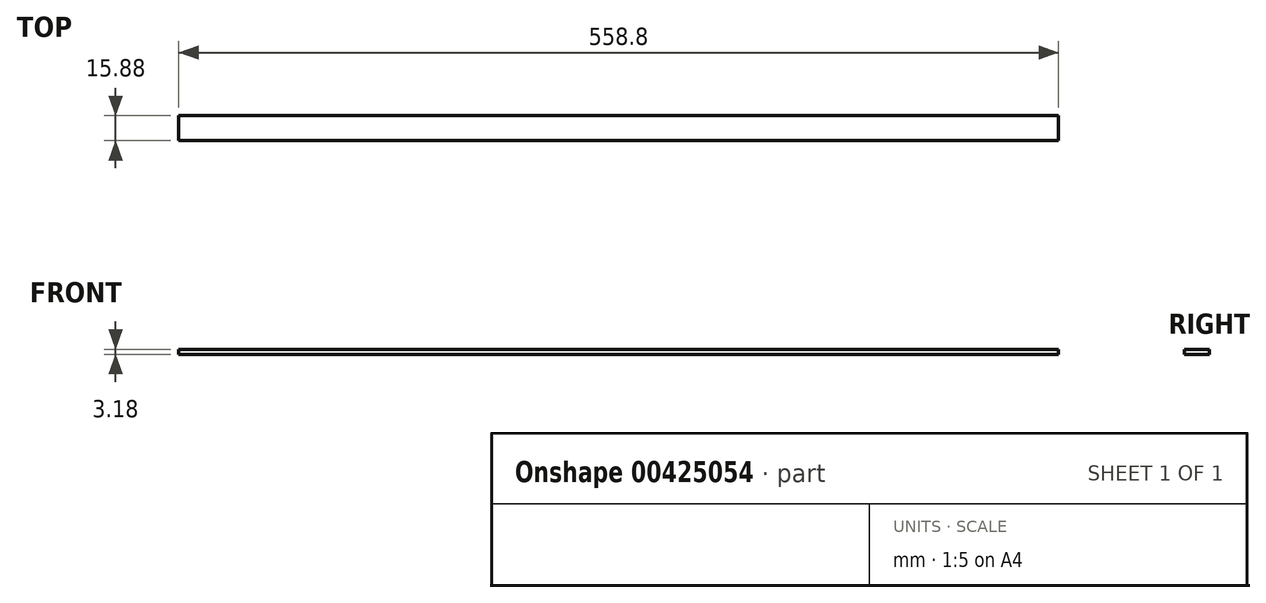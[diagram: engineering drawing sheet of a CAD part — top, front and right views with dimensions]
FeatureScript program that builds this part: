
annotation { "Feature Type Name" : "Feature", "Feature Type Description" : "" }
export const myFeature = defineFeature(function(context is Context, id is Id, definition is map)
    precondition{}
    {
        {
            var Q0;
            Q0=qCreatedBy(makeId("Front.planeOp"),FACE);
            var sketch = newSketch(context, id + "F0", { "sketchPlane" : qUnion([Q0])});
            skLineSegment(sketch, "E0.bottom", {"start": v(-18.6, 23) * mm, "end": v(540.2, 23) * mm});
            skLineSegment(sketch, "E0.top", {"start": v(-18.6, 19.83) * mm, "end": v(540.2, 19.83) * mm});
            skLineSegment(sketch, "E0.left", {"start": v(-18.6, 23) * mm, "end": v(-18.6, 19.83) * mm});
            skLineSegment(sketch, "E0.right", {"start": v(540.2, 23) * mm, "end": v(540.2, 19.83) * mm});
            skSolve(sketch);
        }
        {
            var Q0;
            Q0 = qSketchRegion(id + "F0", true);
            extrude(context, id + "F1", {"entities" : qUnion([Q0]), "depth" : 15.88 * mm});
        }
    });
